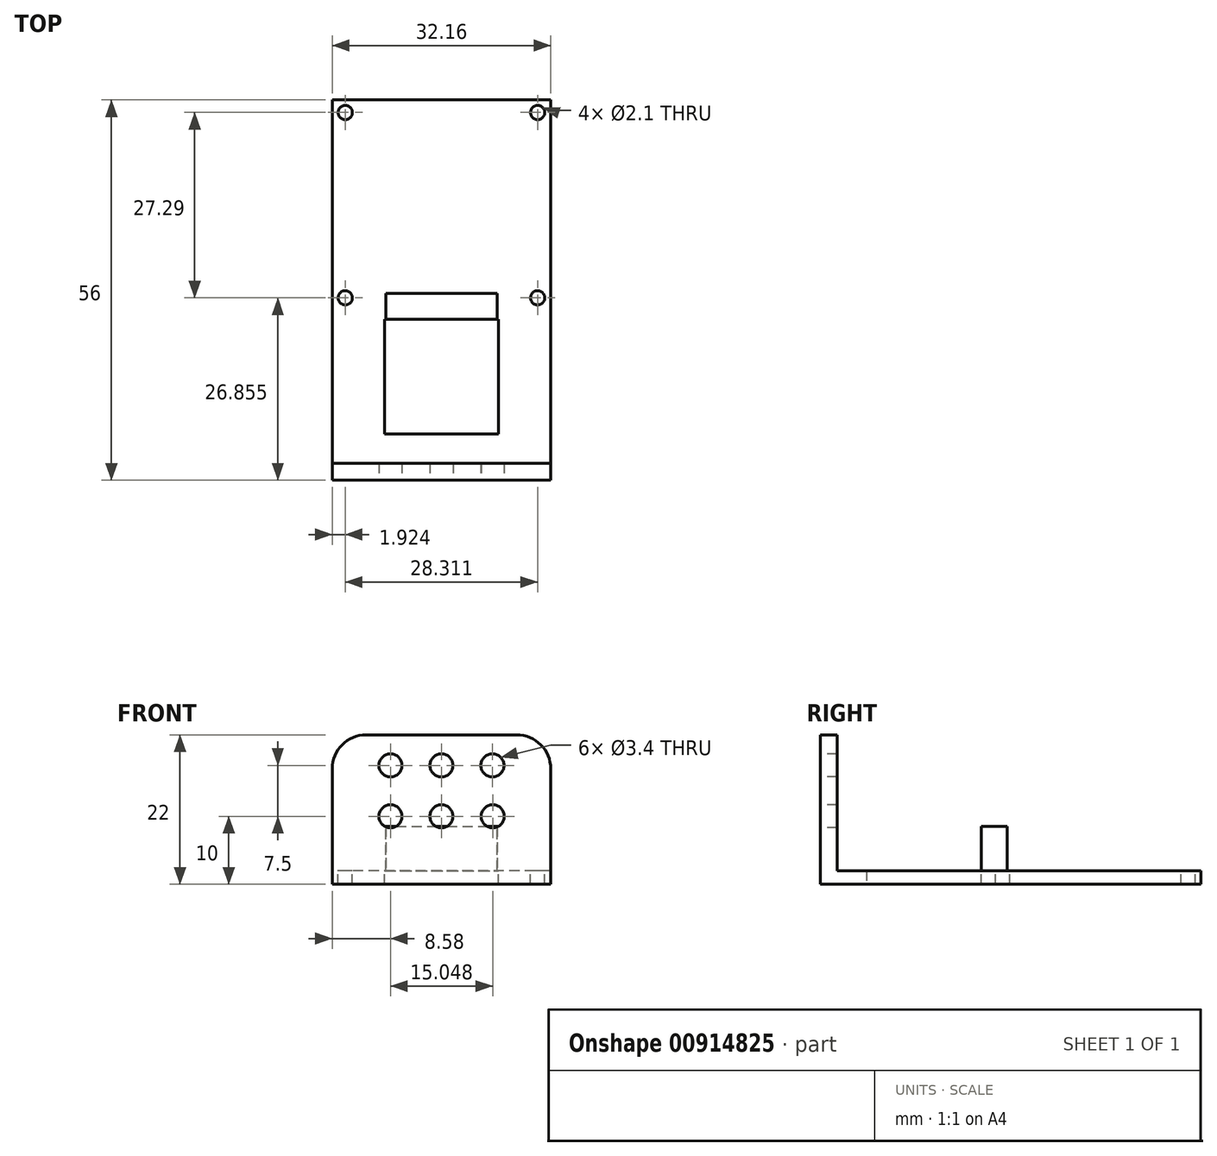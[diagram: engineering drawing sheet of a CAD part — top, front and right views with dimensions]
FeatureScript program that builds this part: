
annotation { "Feature Type Name" : "Feature", "Feature Type Description" : "" }
export const myFeature = defineFeature(function(context is Context, id is Id, definition is map)
    precondition{}
    {
        {
            var Q0;
            Q0=qCreatedBy(makeId("Top.planeOp"),FACE);
            var sketch = newSketch(context, id + "F0", { "sketchPlane" : qUnion([Q0])});
            skLineSegment(sketch, "E0.bottom", {"start": v(16.08, -15.5) * mm, "end": v(-16.08, -15.5) * mm});
            skLineSegment(sketch, "E0.top", {"start": v(16.08, 15.5) * mm, "end": v(-16.08, 15.5) * mm});
            skLineSegment(sketch, "E0.left", {"start": v(16.08, -15.5) * mm, "end": v(16.08, 15.5) * mm});
            skLineSegment(sketch, "E0.right", {"start": v(-16.08, -15.5) * mm, "end": v(-16.08, 15.5) * mm});
            skPoint(sketch, "E0.middle", {"position": v(0, 0) * mm});
            skSolve(sketch);
        }
        {
            var Q0;
            Q0=makeQuery(id+"F0.imprint","IMPRINT",FACE,{"disambiguationData":[TD([[makeQuery(id+"F0.imprint","IMPRINT",EDGE,{"derivedFrom":sQuery(id+"F0.wireOp",EDGE,"E0.bottom")}),-1.0]])]});
            extrude(context, id + "F1", {"entities" : qUnion([Q0]), "depth" : 2 * mm, "offsetDistance" : 25 * mm});
        }
        {
            var Q0;
            Q0=makeQuery(id+"F1.opExtrude","CAP_FACE",FACE,{"disambiguationData":[OSD([sQuery(id+"F0.wireOp",EDGE,"E0.bottom"),sQuery(id+"F0.wireOp",EDGE,"E0.top"),sQuery(id+"F0.wireOp",EDGE,"E0.left"),sQuery(id+"F0.wireOp",EDGE,"E0.right")])],"isStart":false});
            var sketch = newSketch(context, id + "F2", { "sketchPlane" : qUnion([Q0])});
            skLineSegment(sketch, "E1", {"start": v(-16.08, -15.5) * mm, "end": v(16.08, 15.5) * mm});
            skLineSegment(sketch, "E2", {"start": v(16.08, 15.5) * mm, "end": v(16.08, -15.5) * mm});
            skLineSegment(sketch, "E3", {"start": v(16.08, -15.5) * mm, "end": v(-16.08, 15.5) * mm});
            skPoint(sketch, "E4", {"position": v(14.16, 13.64) * mm});
            skPoint(sketch, "E5", {"position": v(-14.16, 13.64) * mm});
            skPoint(sketch, "E6", {"position": v(-14.16, -13.65) * mm});
            skPoint(sketch, "E7", {"position": v(14.16, -13.64) * mm});
            skSolve(sketch);
        }
        {
            var Q0;
            Q0=sQuery(id+"F2.wireOp",VERTEX,"E5");
            var Q1;
            Q1=sQuery(id+"F2.wireOp",VERTEX,"E4");
            var Q2;
            Q2=sQuery(id+"F2.wireOp",VERTEX,"E6");
            var Q3;
            Q3=sQuery(id+"F2.wireOp",VERTEX,"E7");
            var Q4;
            Q4=makeQuery(id+"F1.opExtrude","SWEPT_BODY",BODY,{"disambiguationData":[OSD([sQuery(id+"F0.wireOp",EDGE,"E0.bottom"),sQuery(id+"F0.wireOp",EDGE,"E0.top"),sQuery(id+"F0.wireOp",EDGE,"E0.left"),sQuery(id+"F0.wireOp",EDGE,"E0.right")])]});
            hole(context, id + "F3", {"style" : HoleStyle.SIMPLE, "endStyle" : HoleEndStyle.BLIND, "holeDiameter" : 2.1 * mm, "majorDiameter" : 5 * mm, "holeDepth" : 5 * mm, "isTappedThrough" : true, "tappedDepth" : 12 * mm, "tapClearance" : 3, "startFromSketch" : true, "locations" : qUnion([Q0, Q1, Q2, Q3]), "scope" : qUnion([Q4])});
        }
        {
            var Q0;
            Q0=makeQuery(id+"F1.opExtrude","CAP_FACE",FACE,{"disambiguationData":[OSD([sQuery(id+"F0.wireOp",EDGE,"E0.bottom"),sQuery(id+"F0.wireOp",EDGE,"E0.top"),sQuery(id+"F0.wireOp",EDGE,"E0.left"),sQuery(id+"F0.wireOp",EDGE,"E0.right")])],"isStart":false});
            var sketch = newSketch(context, id + "F4", { "sketchPlane" : qUnion([Q0])});
            skPoint(sketch, "E8", {"position": v(-8.4, -15.5) * mm});
            skPoint(sketch, "E9", {"position": v(0, -15.5) * mm});
            skPoint(sketch, "E10", {"position": v(8.4, -15.5) * mm});
            skPoint(sketch, "E11", {"position": v(8.4, -13) * mm});
            skPoint(sketch, "E12", {"position": v(-5.67, -13) * mm});
            skPoint(sketch, "E13", {"position": v(-8.4, -13) * mm});
            skLineSegment(sketch, "E14", {"start": v(-8.4, -15.5) * mm, "end": v(-8.4, -13) * mm});
            skLineSegment(sketch, "E15", {"start": v(-8.4, -13) * mm, "end": v(8.4, -13) * mm});
            skLineSegment(sketch, "E16", {"start": v(8.4, -13) * mm, "end": v(8.4, -15.5) * mm});
            skSolve(sketch);
        }
        {
            var Q0;
            {var subQ0=sQuery(id+"F4.wireOp",EDGE,"E14");Q0=makeQuery(id+"F4.imprint","IMPRINT",FACE,{"disambiguationData":[TD([[makeQuery(id+"F4.imprint","IMPRINT",EDGE,{"derivedFrom":subQ0}),-1.0]])]});}
            extrude(context, id + "F5", {"entities" : qUnion([Q0]), "operationType" : NewBodyOperationType.ADD, "depth" : 6.5 * mm, "offsetDistance" : 25 * mm});
        }
        {
            var Q0;
            {var subQ0=sQuery(id+"F0.wireOp",EDGE,"E0.bottom");Q0=makeQuery(id+"F5.boolean.opBoolean","MERGE",FACE,{"derivedFrom":[makeQuery(id+"F1.opExtrude","SWEPT_FACE",FACE,{"disambiguationData":[OSD([subQ0])]}),makeQuery(id+"F5.opExtrude","SWEPT_FACE",FACE,{"disambiguationData":[OSD([subQ0])]})]});}
            extrude(context, id + "F6", {"entities" : qUnion([Q0]), "operationType" : NewBodyOperationType.ADD, "depth" : 25 * mm, "offsetDistance" : 25 * mm});
        }
        {
            var Q0;
            {var subQ0=sQuery(id+"F0.wireOp",EDGE,"E0.bottom");Q0=makeQuery(id+"F6.boolean.opBoolean","MERGE",FACE,{"derivedFrom":[makeQuery(id+"F5.opExtrude","CAP_FACE",FACE,{"disambiguationData":[OSD([subQ0,sQuery(id+"F4.wireOp",EDGE,"E14"),sQuery(id+"F4.wireOp",EDGE,"E15"),sQuery(id+"F4.wireOp",EDGE,"E16")])],"isStart":false}),makeQuery(id+"F6.opExtrude","SWEPT_FACE",FACE,{"disambiguationData":[OSD([subQ0]),TDD([makeQuery(id+"F5.opExtrude","CAP_EDGE",EDGE,{"disambiguationData":[OSD([subQ0])],"isStart":false})])]})]});}
            var sketch = newSketch(context, id + "F7", { "sketchPlane" : qUnion([Q0])});
            skPoint(sketch, "E17", {"position": v(0, -16.78) * mm});
            skPoint(sketch, "E18", {"position": v(-8.4, -16.78) * mm});
            skPoint(sketch, "E19", {"position": v(8.4, -16.78) * mm});
            skLineSegment(sketch, "E20", {"start": v(-8.4, -16.78) * mm, "end": v(8.4, -16.78) * mm});
            skSolve(sketch);
        }
        {
            var Q0;
            {var subQ0=sQuery(id+"F7.wireOp",EDGE,"E20");Q0=makeQuery(id+"F7.imprint","IMPRINT",FACE,{"disambiguationData":[TD([[makeQuery(id+"F7.imprint","IMPRINT",EDGE,{"derivedFrom":subQ0}),-1.0]])]});}
            extrude(context, id + "F8", {"entities" : qUnion([Q0]), "operationType" : NewBodyOperationType.REMOVE, "oppositeDirection" : true, "depth" : 25 * mm, "offsetDistance" : 25 * mm});
        }
        {
            var Q0;
            Q0=makeQuery(id+"F8.boolean.opBoolean","COPY",FACE,{"derivedFrom":makeQuery(id+"F8.opExtrude","SWEPT_FACE",FACE,{"disambiguationData":[OSD([sQuery(id+"F0.wireOp",EDGE,"E0.bottom"),sQuery(id+"F4.wireOp",EDGE,"E16")])]})});
            var sketch = newSketch(context, id + "F9", { "sketchPlane" : qUnion([Q0])});
            skPoint(sketch, "E21", {"position": v(33.68, 1) * mm});
            skPoint(sketch, "E22", {"position": v(33.68, 2) * mm});
            skPoint(sketch, "E23", {"position": v(33.68, 0) * mm});
            skLineSegment(sketch, "E24", {"start": v(33.68, 2) * mm, "end": v(33.68, 0) * mm});
            skSolve(sketch);
        }
        {
            var Q0;
            {var subQ0=sQuery(id+"F9.wireOp",EDGE,"E24");Q0=makeQuery(id+"F9.imprint","IMPRINT",FACE,{"disambiguationData":[TD([[makeQuery(id+"F9.imprint","IMPRINT",EDGE,{"derivedFrom":subQ0}),1.0]])]});}
            extrude(context, id + "F10", {"entities" : qUnion([Q0]), "operationType" : NewBodyOperationType.ADD, "depth" : 18 * mm, "offsetDistance" : 25 * mm});
        }
        {
            var Q0;
            {var subQ0=sQuery(id+"F0.wireOp",EDGE,"E0.right");var subQ1=sQuery(id+"F0.wireOp",EDGE,"E0.left");var subQ2=sQuery(id+"F0.wireOp",EDGE,"E0.top");var subQ3=sQuery(id+"F0.wireOp",EDGE,"E0.bottom");Q0=makeQuery(id+"F10.boolean.opBoolean","MERGE",FACE,{"derivedFrom":[makeQuery(id+"F6.boolean.opBoolean","MERGE",FACE,{"derivedFrom":[makeQuery(id+"F1.opExtrude","CAP_FACE",FACE,{"disambiguationData":[OSD([subQ3,subQ2,subQ1,subQ0])],"isStart":true}),makeQuery(id+"F6.opExtrude","SWEPT_FACE",FACE,{"disambiguationData":[OSD([subQ3]),TDD([makeQuery(id+"F1.opExtrude","CAP_EDGE",EDGE,{"disambiguationData":[OSD([subQ3])],"isStart":true})])]})]}),makeQuery(id+"F10.opExtrude","SWEPT_FACE",FACE,{"disambiguationData":[OSD([subQ3,subQ2,subQ1,subQ0,sQuery(id+"F4.wireOp",EDGE,"E16")])]})]});}
            var sketch = newSketch(context, id + "F11", { "sketchPlane" : qUnion([Q0])});
            skPoint(sketch, "E25", {"position": v(0, 38) * mm});
            skPoint(sketch, "E25.positionSnap0", {"position": v(0, 40.5) * mm});
            skPoint(sketch, "E26", {"position": v(-16.08, 38) * mm});
            skPoint(sketch, "E27", {"position": v(16.08, 38) * mm});
            skLineSegment(sketch, "E28", {"start": v(-16.08, 38) * mm, "end": v(16.08, 38) * mm});
            skSolve(sketch);
        }
        {
            var Q0;
            {var subQ0=sQuery(id+"F11.wireOp",EDGE,"E28");Q0=makeQuery(id+"F11.imprint","IMPRINT",FACE,{"disambiguationData":[TD([[makeQuery(id+"F11.imprint","IMPRINT",EDGE,{"derivedFrom":subQ0}),1.0]])]});}
            extrude(context, id + "F12", {"entities" : qUnion([Q0]), "operationType" : NewBodyOperationType.ADD, "oppositeDirection" : true, "depth" : 22 * mm, "offsetDistance" : 25 * mm});
        }
        {
            var Q0;
            {var subQ0=sQuery(id+"F4.wireOp",EDGE,"E16");var subQ1=sQuery(id+"F0.wireOp",EDGE,"E0.right");var subQ2=sQuery(id+"F0.wireOp",EDGE,"E0.left");var subQ3=sQuery(id+"F0.wireOp",EDGE,"E0.top");var subQ4=sQuery(id+"F0.wireOp",EDGE,"E0.bottom");var subQ5=makeQuery(id+"F1.opExtrude","SWEPT_FACE",FACE,{"disambiguationData":[OSD([subQ1])]});var subQ14=makeQuery(id+"F1.opExtrude","SWEPT_FACE",FACE,{"disambiguationData":[OSD([subQ2])]});var subQ16=makeQuery(id+"F6.opExtrude","CAP_FACE",FACE,{"disambiguationData":[OSD([subQ4])],"isStart":false});Q0=makeQuery(id+"F12.boolean.opBoolean","MERGE",FACE,{"derivedFrom":[makeQuery(id+"F10.boolean.opBoolean","MERGE",FACE,{"derivedFrom":[makeQuery(id+"F8.boolean.opBoolean","SPLIT",FACE,{"disambiguationData":[TD([subQ14])],"derivedFrom":subQ16}),makeQuery(id+"F8.boolean.opBoolean","SPLIT",FACE,{"disambiguationData":[TD([subQ5])],"derivedFrom":subQ16}),makeQuery(id+"F10.opExtrude","SWEPT_FACE",FACE,{"disambiguationData":[OSD([subQ4,subQ0]),TDD([makeQuery(id+"F9.imprint","IMPRINT",EDGE,{"derivedFrom":makeQuery(id+"F8.boolean.opBoolean","COPY",EDGE,{"derivedFrom":makeQuery(id+"F8.opExtrude","SWEPT_EDGE",EDGE,{"disambiguationData":[OSD([subQ4,subQ0])]})})})])]})]}),makeQuery(id+"F12.opExtrude","SWEPT_FACE",FACE,{"disambiguationData":[OSD([subQ4,subQ3,subQ2,subQ1,subQ0])]})]});}
            var sketch = newSketch(context, id + "F13", { "sketchPlane" : qUnion([Q0])});
            skPoint(sketch, "E29", {"position": v(0, 17.5) * mm});
            skPoint(sketch, "E30", {"position": v(0, 10) * mm});
            skPoint(sketch, "E31", {"position": v(7.55, 10) * mm});
            skPoint(sketch, "E32", {"position": v(7.5, 17.5) * mm});
            skPoint(sketch, "E33", {"position": v(-7.5, 10) * mm});
            skPoint(sketch, "E34", {"position": v(-7.5, 17.5) * mm});
            skSolve(sketch);
        }
        {
            var Q0;
            Q0=sQuery(id+"F13.wireOp",VERTEX,"E34");
            var Q1;
            Q1=sQuery(id+"F13.wireOp",VERTEX,"E33");
            var Q2;
            Q2=sQuery(id+"F13.wireOp",VERTEX,"E30");
            var Q3;
            Q3=sQuery(id+"F13.wireOp",VERTEX,"E29");
            var Q4;
            Q4=sQuery(id+"F13.wireOp",VERTEX,"E32");
            var Q5;
            Q5=sQuery(id+"F13.wireOp",VERTEX,"E31");
            var Q6;
            Q6=makeQuery(id+"F1.opExtrude","SWEPT_BODY",BODY,{"disambiguationData":[OSD([sQuery(id+"F0.wireOp",EDGE,"E0.bottom"),sQuery(id+"F0.wireOp",EDGE,"E0.top"),sQuery(id+"F0.wireOp",EDGE,"E0.left"),sQuery(id+"F0.wireOp",EDGE,"E0.right")])]});
            hole(context, id + "F14", {"style" : HoleStyle.SIMPLE, "endStyle" : HoleEndStyle.BLIND, "standardTappedOrClearance" : lookupTablePath({ "fit" : "Normal", "standard" : "ISO", "size" : "M3", "type" : "Clearance" }), "standardBlindInLast" : lookupTablePath({ "fit" : "Normal", "standard" : "ISO", "engagement" : "75%", "pitch" : "0.5 mm", "size" : "M3", "type" : "Clearance & tapped" }), "holeDiameter" : 3.4 * mm, "majorDiameter" : 5 * mm, "holeDepth" : 5 * mm, "isTappedThrough" : true, "tappedDepth" : 12 * mm, "tapClearance" : 3, "startFromSketch" : true, "locations" : qUnion([Q0, Q1, Q2, Q3, Q4, Q5]), "scope" : qUnion([Q6])});
        }
        {
            var Q0;
            {var subQ0=sQuery(id+"F4.wireOp",EDGE,"E16");Q0=makeQuery(id+"F6.boolean.opBoolean","MERGE",FACE,{"derivedFrom":[makeQuery(id+"F5.opExtrude","SWEPT_FACE",FACE,{"disambiguationData":[OSD([subQ0])]}),makeQuery(id+"F6.opExtrude","SWEPT_FACE",FACE,{"disambiguationData":[OSD([sQuery(id+"F0.wireOp",EDGE,"E0.bottom"),subQ0])]})]});}
            extrude(context, id + "F15", {"entities" : qUnion([Q0]), "operationType" : NewBodyOperationType.REMOVE, "oppositeDirection" : true, "depth" : 0.2 * mm, "offsetDistance" : 25 * mm});
        }
        {
            var Q0;
            {var subQ0=sQuery(id+"F4.wireOp",EDGE,"E14");Q0=makeQuery(id+"F6.boolean.opBoolean","MERGE",FACE,{"derivedFrom":[makeQuery(id+"F5.opExtrude","SWEPT_FACE",FACE,{"disambiguationData":[OSD([subQ0])]}),makeQuery(id+"F6.opExtrude","SWEPT_FACE",FACE,{"disambiguationData":[OSD([sQuery(id+"F0.wireOp",EDGE,"E0.bottom"),subQ0])]})]});}
            extrude(context, id + "F16", {"entities" : qUnion([Q0]), "operationType" : NewBodyOperationType.REMOVE, "oppositeDirection" : true, "depth" : 0.2 * mm, "offsetDistance" : 25 * mm});
        }
        {
            var Q0;
            Q0=makeQuery(id+"F12.opExtrude","CAP_EDGE",EDGE,{"disambiguationData":[OSD([sQuery(id+"F0.wireOp",EDGE,"E0.bottom"),sQuery(id+"F0.wireOp",EDGE,"E0.right")])],"isStart":false});
            var Q1;
            Q1=makeQuery(id+"F12.opExtrude","CAP_EDGE",EDGE,{"disambiguationData":[OSD([sQuery(id+"F0.wireOp",EDGE,"E0.bottom"),sQuery(id+"F0.wireOp",EDGE,"E0.left")])],"isStart":false});
            fillet(context, id + "F17", {"entities" : qUnion([Q0, Q1]), "tangentPropagation" : true, "radius" : 5 * mm, "defaultsChanged" : false, "vertexSettings" : [], "allowEdgeOverflow" : false});
        }
    });
